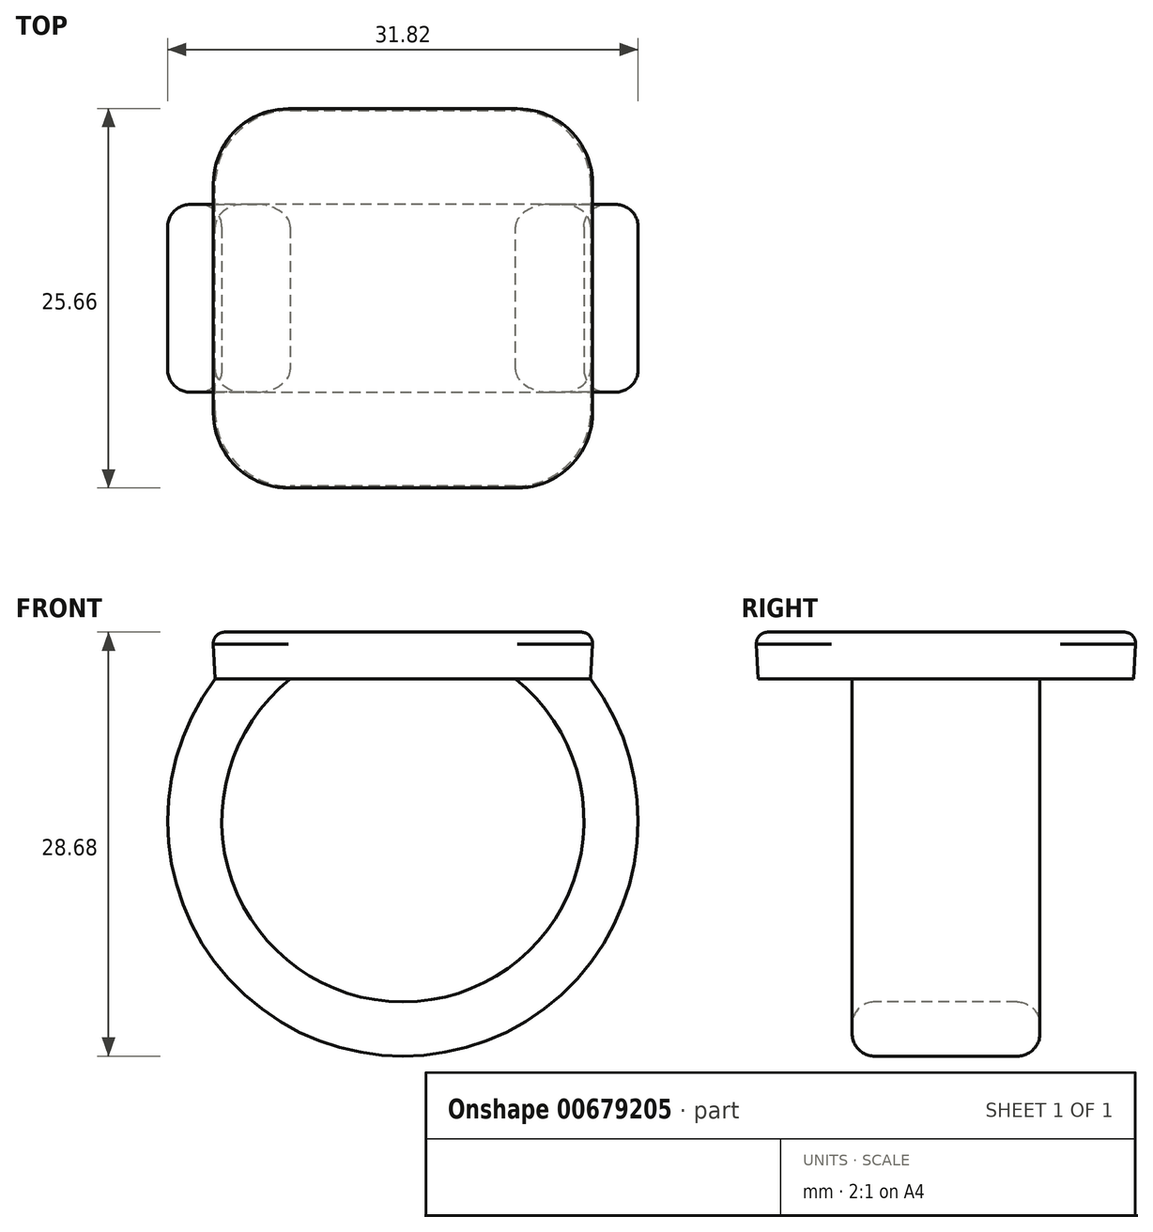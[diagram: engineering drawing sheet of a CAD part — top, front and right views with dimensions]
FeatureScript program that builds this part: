
annotation { "Feature Type Name" : "Feature", "Feature Type Description" : "" }
export const myFeature = defineFeature(function(context is Context, id is Id, definition is map)
    precondition{}
    {
        {
            var Q0;
            Q0=qCreatedBy(makeId("Top.planeOp"),FACE);
            var sketch = newSketch(context, id + "F0", { "sketchPlane" : qUnion([Q0])});
            skLineSegment(sketch, "E0.bottom", {"start": v(12.7, 12.7) * mm, "end": v(-12.7, 12.7) * mm});
            skLineSegment(sketch, "E0.top", {"start": v(12.7, -12.7) * mm, "end": v(-12.7, -12.7) * mm});
            skLineSegment(sketch, "E0.left", {"start": v(12.7, 12.7) * mm, "end": v(12.7, -12.7) * mm});
            skLineSegment(sketch, "E0.right", {"start": v(-12.7, 12.7) * mm, "end": v(-12.7, -12.7) * mm});
            skPoint(sketch, "E0.middle", {"position": v(0, 0) * mm});
            skSolve(sketch);
        }
        {
            var Q0;
            Q0 = qSketchRegion(id + "F0", true);
            extrude(context, id + "F1", {"entities" : qUnion([Q0]), "depth" : 3.17 * mm, "offsetDistance" : 25.4 * mm, "hasDraft" : true, "draftAngle" : 3 * degree});
        }
        {
            var Q0;
            Q0=qCreatedBy(makeId("Front.planeOp"),FACE);
            var sketch = newSketch(context, id + "F2", { "sketchPlane" : qUnion([Q0])});
            skArc(sketch, "E1", {"start": v(-10.16, 0) * mm, "mid": v(0, -23.56) * mm, "end": v(10.16, 0) * mm});
            skSolve(sketch);
        }
        {
            var Q0;
            Q0=makeQuery(id+"F1.opExtrude","CAP_FACE",FACE,{"disambiguationData":[OSD([sQuery(id+"F0.wireOp",EDGE,"E0.bottom"),sQuery(id+"F0.wireOp",EDGE,"E0.top"),sQuery(id+"F0.wireOp",EDGE,"E0.left"),sQuery(id+"F0.wireOp",EDGE,"E0.right")])],"isStart":true});
            var sketch = newSketch(context, id + "F3", { "sketchPlane" : qUnion([Q0])});
            skLineSegment(sketch, "E2.bottom", {"start": v(-7.62, -6.35) * mm, "end": v(-12.7, -6.35) * mm});
            skLineSegment(sketch, "E2.top", {"start": v(-7.62, 6.35) * mm, "end": v(-12.7, 6.35) * mm});
            skLineSegment(sketch, "E2.left", {"start": v(-7.62, -6.35) * mm, "end": v(-7.62, 6.35) * mm});
            skLineSegment(sketch, "E2.right", {"start": v(-12.7, -6.35) * mm, "end": v(-12.7, 6.35) * mm});
            skPoint(sketch, "E2.middle", {"position": v(-10.16, 0) * mm});
            skSolve(sketch);
        }
        {
            var Q0;
            Q0 = qSketchRegion(id + "F3", true);
            var Q1;
            Q1 = qConstructionFilter(qBodyType(qCreatedBy(id + "F2" ,EDGE), BodyType.WIRE), ConstructionObject.NO);
            sweep(context, id + "F4", {"operationType" : NewBodyOperationType.ADD, "profiles" : qUnion([Q0]), "path" : qUnion([Q1])});
        }
        {
            var Q0;
            Q0=qCreatedBy(makeId("Front.planeOp"),FACE);
            var sketch = newSketch(context, id + "F5", { "sketchPlane" : qUnion([Q0])});
            skArc(sketch, "E3.0", {"start": v(10.01, -2.54) * mm, "mid": v(8.9, -1.18) * mm, "end": v(7.62, 0) * mm});
            skLineSegment(sketch, "E3.1", {"start": v(10.01, -2.54) * mm, "end": v(10.16, 0) * mm});
            skLineSegment(sketch, "E3.2", {"start": v(10.16, 0) * mm, "end": v(7.62, 0) * mm});
            skPoint(sketch, "E4.trimOffspring.end.orphan", {"position": v(-12.7, 0) * mm});
            skPoint(sketch, "E4.trimOffspring.start.orphan", {"position": v(-7.62, 0) * mm});
            skPoint(sketch, "E5.orphan", {"position": v(12.7, 0) * mm});
            skSolve(sketch);
        }
        {
            var Q0;
            Q0 = qSketchRegion(id + "F5", true);
            var Q1;
            Q1=makeQuery(id+"F4.opSweep","SWEPT_FACE",FACE,{"disambiguationData":[OSD([sQuery(id+"F2.wireOp",EDGE,"E1"),sQuery(id+"F3.wireOp",EDGE,"E2.top")])]});
            var Q2;
            Q2=makeQuery(id+"F4.opSweep","SWEPT_FACE",FACE,{"disambiguationData":[OSD([sQuery(id+"F2.wireOp",EDGE,"E1"),sQuery(id+"F3.wireOp",EDGE,"E2.bottom")])]});
            extrude(context, id + "F6", {"entities" : qUnion([Q0]), "operationType" : NewBodyOperationType.ADD, "endBound" : BoundingType.UP_TO_SURFACE, "depth" : 25.4 * mm, "endBoundEntityFace" : qUnion([Q1]), "offsetDistance" : 25.4 * mm, "hasSecondDirection" : true, "secondDirectionBound" : SecondDirectionBoundingType.UP_TO_SURFACE, "secondDirectionOppositeDirection" : true, "secondDirectionDepth" : 25.4 * mm, "secondDirectionBoundEntityFace" : qUnion([Q2])});
        }
        {
            var Q0;
            Q0=makeQuery(id+"F1.opExtrude","SWEPT_EDGE",EDGE,{"disambiguationData":[OSD([sQuery(id+"F0.wireOp",EDGE,"E0.top"),sQuery(id+"F0.wireOp",EDGE,"E0.left")])]});
            var Q1;
            Q1=makeQuery(id+"F1.opExtrude","SWEPT_EDGE",EDGE,{"disambiguationData":[OSD([sQuery(id+"F0.wireOp",EDGE,"E0.bottom"),sQuery(id+"F0.wireOp",EDGE,"E0.left")])]});
            var Q2;
            Q2=makeQuery(id+"F1.opExtrude","SWEPT_EDGE",EDGE,{"disambiguationData":[OSD([sQuery(id+"F0.wireOp",EDGE,"E0.bottom"),sQuery(id+"F0.wireOp",EDGE,"E0.right")])]});
            var Q3;
            Q3=makeQuery(id+"F1.opExtrude","SWEPT_EDGE",EDGE,{"disambiguationData":[OSD([sQuery(id+"F0.wireOp",EDGE,"E0.top"),sQuery(id+"F0.wireOp",EDGE,"E0.right")])]});
            fillet(context, id + "F7", {"entities" : qUnion([Q0, Q1, Q2, Q3]), "radius" : 5.08 * mm, "tangentPropagation" : true, "allowEdgeOverflow" : false});
        }
        {
            var Q0;
            {var subQ0=sQuery(id+"F3.wireOp",EDGE,"E2.bottom");var subQ1=sQuery(id+"F2.wireOp",EDGE,"E1");Q0=makeQuery(id+"F6.boolean.opBoolean","MERGE",EDGE,{"derivedFrom":[makeQuery(id+"F4.opSweep","SWEPT_EDGE",EDGE,{"disambiguationData":[OSD([subQ1,subQ0,sQuery(id+"F3.wireOp",EDGE,"E2.left")])]}),makeQuery(id+"F6.opExtrude","TWEAK_EDGE",EDGE,{"derivedFrom":[makeQuery(id+"F4.opSweep","SWEPT_FACE",FACE,{"disambiguationData":[OSD([subQ1,subQ0])]}),makeQuery(id+"F5.imprint","IMPRINT",EDGE,{"derivedFrom":sQuery(id+"F5.wireOp",EDGE,"E3.0")})]})]});}
            var Q1;
            Q1=makeQuery(id+"F4.opSweep","SWEPT_EDGE",EDGE,{"disambiguationData":[OSD([sQuery(id+"F0.wireOp",EDGE,"E0.right"),sQuery(id+"F2.wireOp",EDGE,"E1"),sQuery(id+"F3.wireOp",EDGE,"E2.bottom"),sQuery(id+"F3.wireOp",EDGE,"E2.right")])]});
            var Q2;
            {var subQ0=sQuery(id+"F3.wireOp",EDGE,"E2.top");var subQ1=sQuery(id+"F2.wireOp",EDGE,"E1");Q2=makeQuery(id+"F6.boolean.opBoolean","MERGE",EDGE,{"derivedFrom":[makeQuery(id+"F4.opSweep","SWEPT_EDGE",EDGE,{"disambiguationData":[OSD([subQ1,subQ0,sQuery(id+"F3.wireOp",EDGE,"E2.left")])]}),makeQuery(id+"F6.opExtrude","TWEAK_EDGE",EDGE,{"derivedFrom":[makeQuery(id+"F4.opSweep","SWEPT_FACE",FACE,{"disambiguationData":[OSD([subQ1,subQ0])]}),makeQuery(id+"F5.imprint","IMPRINT",EDGE,{"derivedFrom":sQuery(id+"F5.wireOp",EDGE,"E3.0")})]})]});}
            var Q3;
            Q3=makeQuery(id+"F4.opSweep","SWEPT_EDGE",EDGE,{"disambiguationData":[OSD([sQuery(id+"F0.wireOp",EDGE,"E0.right"),sQuery(id+"F2.wireOp",EDGE,"E1"),sQuery(id+"F3.wireOp",EDGE,"E2.top"),sQuery(id+"F3.wireOp",EDGE,"E2.right")])]});
            fillet(context, id + "F8", {"entities" : qUnion([Q0, Q1, Q2, Q3]), "radius" : 1.52 * mm, "tangentPropagation" : true, "allowEdgeOverflow" : false});
        }
        {
            var Q0;
            Q0=makeQuery(id+"F1.opExtrude","CAP_FACE",FACE,{"disambiguationData":[OSD([sQuery(id+"F0.wireOp",EDGE,"E0.bottom"),sQuery(id+"F0.wireOp",EDGE,"E0.top"),sQuery(id+"F0.wireOp",EDGE,"E0.left"),sQuery(id+"F0.wireOp",EDGE,"E0.right")])],"isStart":false});
            fillet(context, id + "F9", {"entities" : qUnion([Q0]), "radius" : 0.76 * mm, "tangentPropagation" : true, "allowEdgeOverflow" : false});
        }
    });
